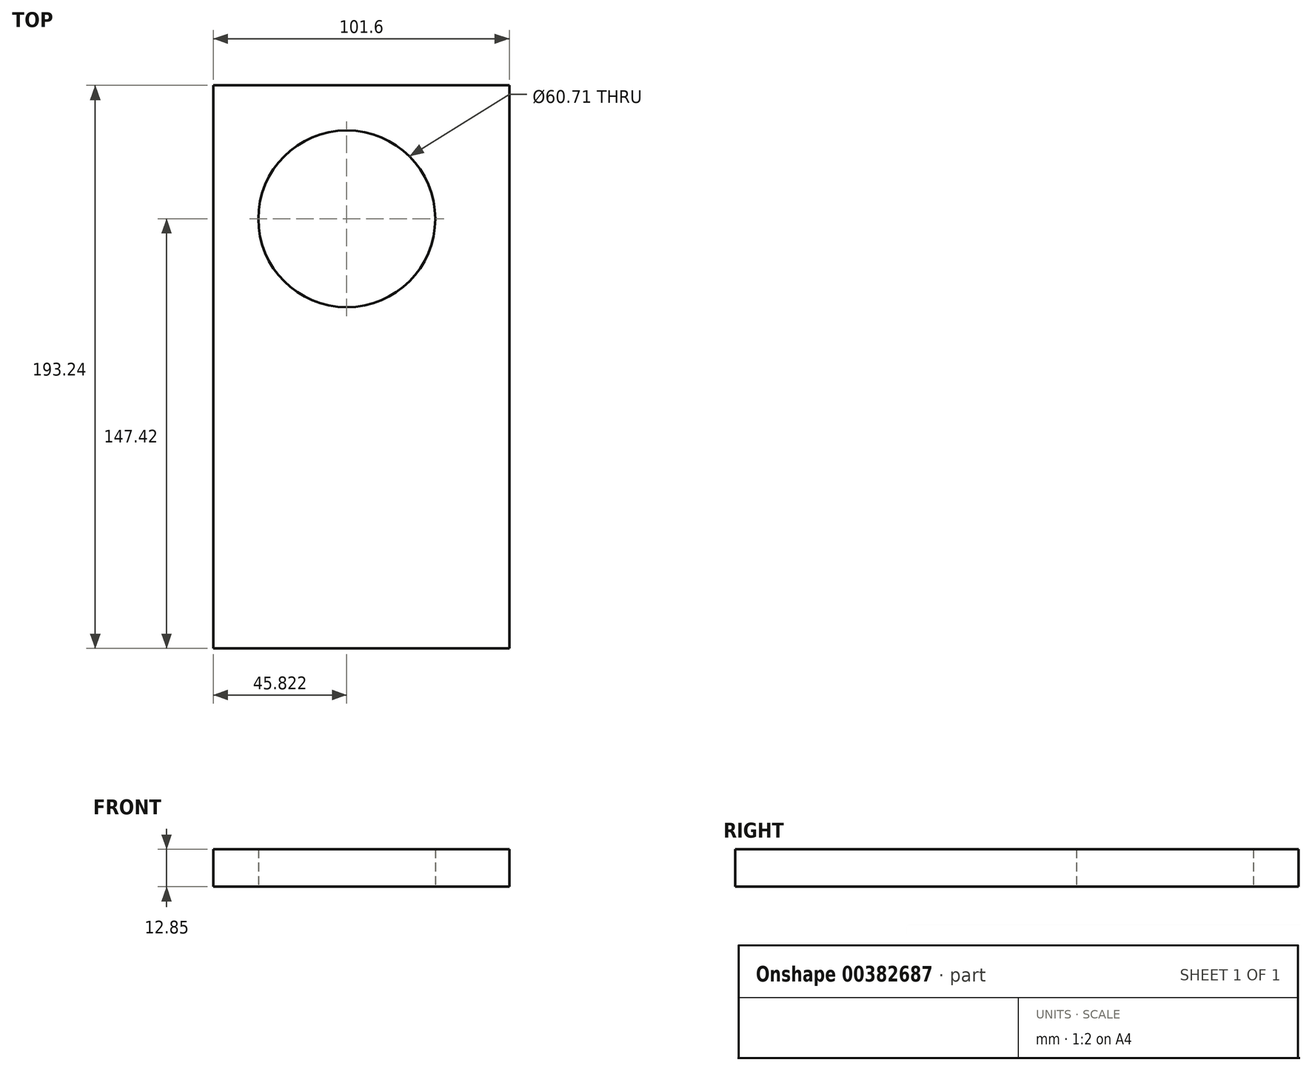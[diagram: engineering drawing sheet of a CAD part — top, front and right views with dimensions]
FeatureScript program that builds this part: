
annotation { "Feature Type Name" : "Feature", "Feature Type Description" : "" }
export const myFeature = defineFeature(function(context is Context, id is Id, definition is map)
    precondition{}
    {
        {
            var Q0;
            Q0=qCreatedBy(makeId("Top.planeOp"),FACE);
            var sketch = newSketch(context, id + "F0", { "sketchPlane" : qUnion([Q0])});
            skLineSegment(sketch, "E0.bottom", {"start": v(0, 86.14) * mm, "end": v(-101.6, 86.14) * mm});
            skLineSegment(sketch, "E0.top", {"start": v(0, -107.1) * mm, "end": v(-101.6, -107.1) * mm});
            skLineSegment(sketch, "E0.left", {"start": v(0, 86.14) * mm, "end": v(0, -107.1) * mm});
            skLineSegment(sketch, "E0.right", {"start": v(-101.6, 86.14) * mm, "end": v(-101.6, -107.1) * mm});
            skSolve(sketch);
        }
        {
            var Q0;
            Q0=makeQuery(id+"F0.imprint","IMPRINT",FACE,{"disambiguationData":[TD([[makeQuery(id+"F0.imprint","IMPRINT",EDGE,{"derivedFrom":sQuery(id+"F0.wireOp",EDGE,"E0.bottom")}),1.0]])]});
            var sketch = newSketch(context, id + "F1", { "sketchPlane" : qUnion([Q0])});
            skCircle(sketch, "E1", {"center": v(-55.78, 40.32) * mm, "radius": 30.35 * mm});
            skSolve(sketch);
        }
        {
            var Q0;
            Q0=makeQuery(id+"F0.imprint","IMPRINT",FACE,{"disambiguationData":[TD([[makeQuery(id+"F0.imprint","IMPRINT",EDGE,{"derivedFrom":sQuery(id+"F0.wireOp",EDGE,"E0.bottom")}),1.0]])]});
            var sketch = newSketch(context, id + "F2", { "sketchPlane" : qUnion([Q0])});
            skCircle(sketch, "E2.0", {"center": v(-55.78, 40.32) * mm, "radius": 30.35 * mm});
            skLineSegment(sketch, "E3.0.0", {"start": v(-101.6, -107.1) * mm, "end": v(0, -107.1) * mm});
            skLineSegment(sketch, "E3.0.1", {"start": v(0, -107.1) * mm, "end": v(0, 86.14) * mm});
            skLineSegment(sketch, "E3.0.2", {"start": v(0, 86.14) * mm, "end": v(-101.6, 86.14) * mm});
            skLineSegment(sketch, "E3.0.3", {"start": v(-101.6, 86.14) * mm, "end": v(-101.6, -107.1) * mm});
            skSolve(sketch);
        }
        {
            var Q0;
            Q0=qSketchRegion(id+"F2",true);
            extrude(context, id + "F3", {"entities" : qUnion([Q0]), "depth" : 12.85 * mm});
        }
    });
